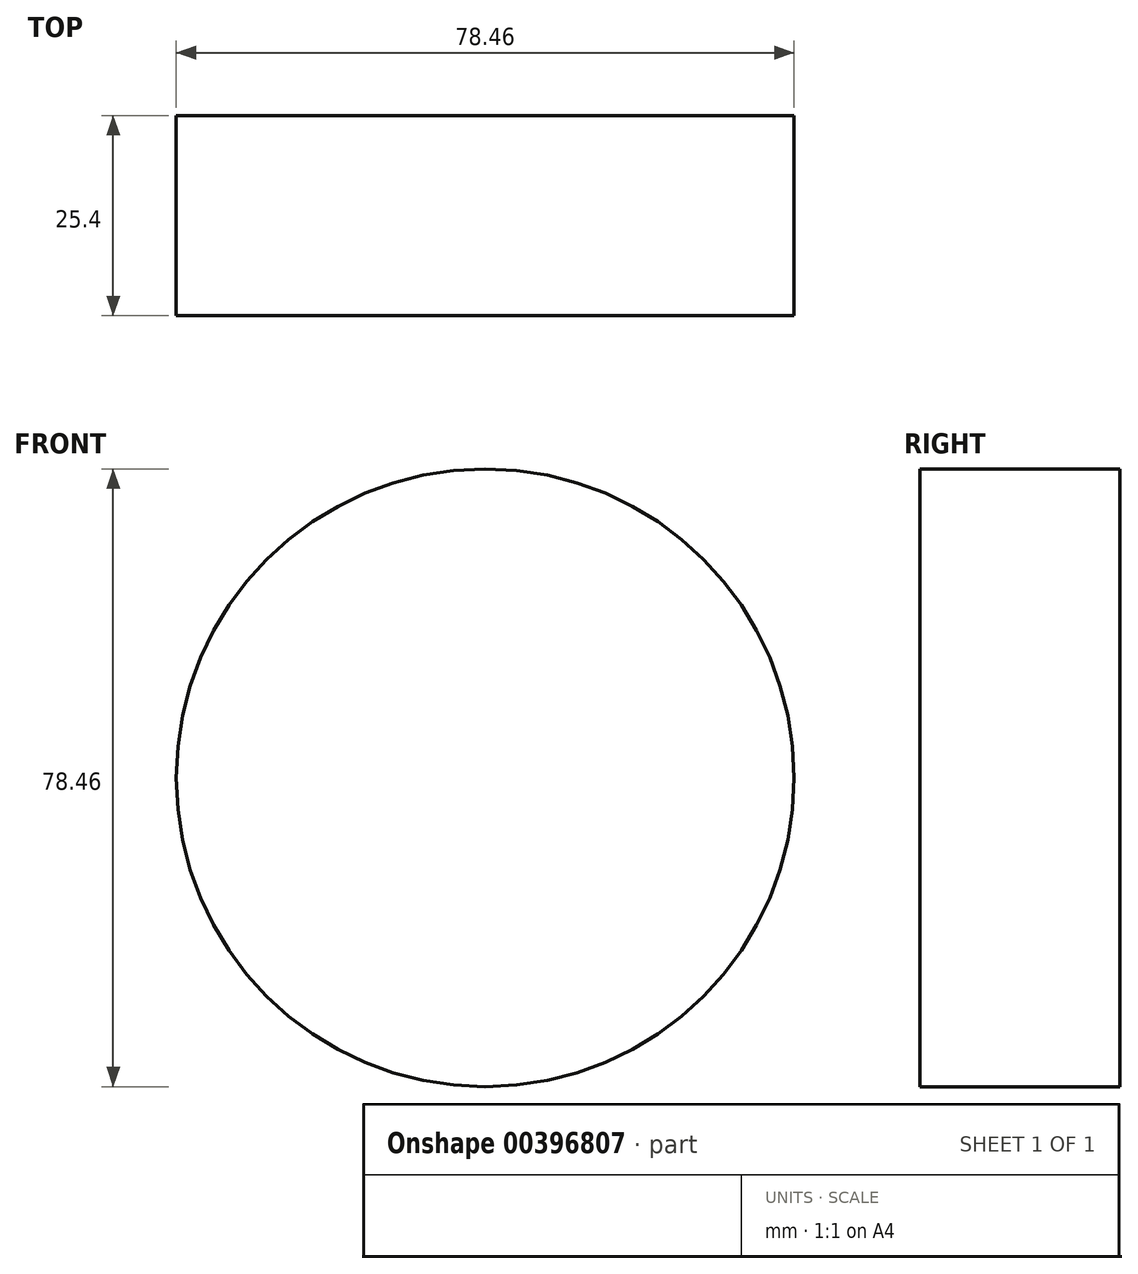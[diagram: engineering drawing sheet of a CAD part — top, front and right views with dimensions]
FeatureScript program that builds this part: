
annotation { "Feature Type Name" : "Feature", "Feature Type Description" : "" }
export const myFeature = defineFeature(function(context is Context, id is Id, definition is map)
    precondition{}
    {
        {
            var Q0;
            Q0=qCreatedBy(makeId("Front.planeOp"),FACE);
            var sketch = newSketch(context, id + "F0", { "sketchPlane" : qUnion([Q0])});
            skCircle(sketch, "E0", {"center": v(0, 0) * mm, "radius": 39.23 * mm});
            skSolve(sketch);
        }
        {
            var Q0;
            Q0 = qSketchRegion(id + "F0", true);
            extrude(context, id + "F1", {"entities" : qUnion([Q0]), "depth" : 25.4 * mm});
        }
    });
